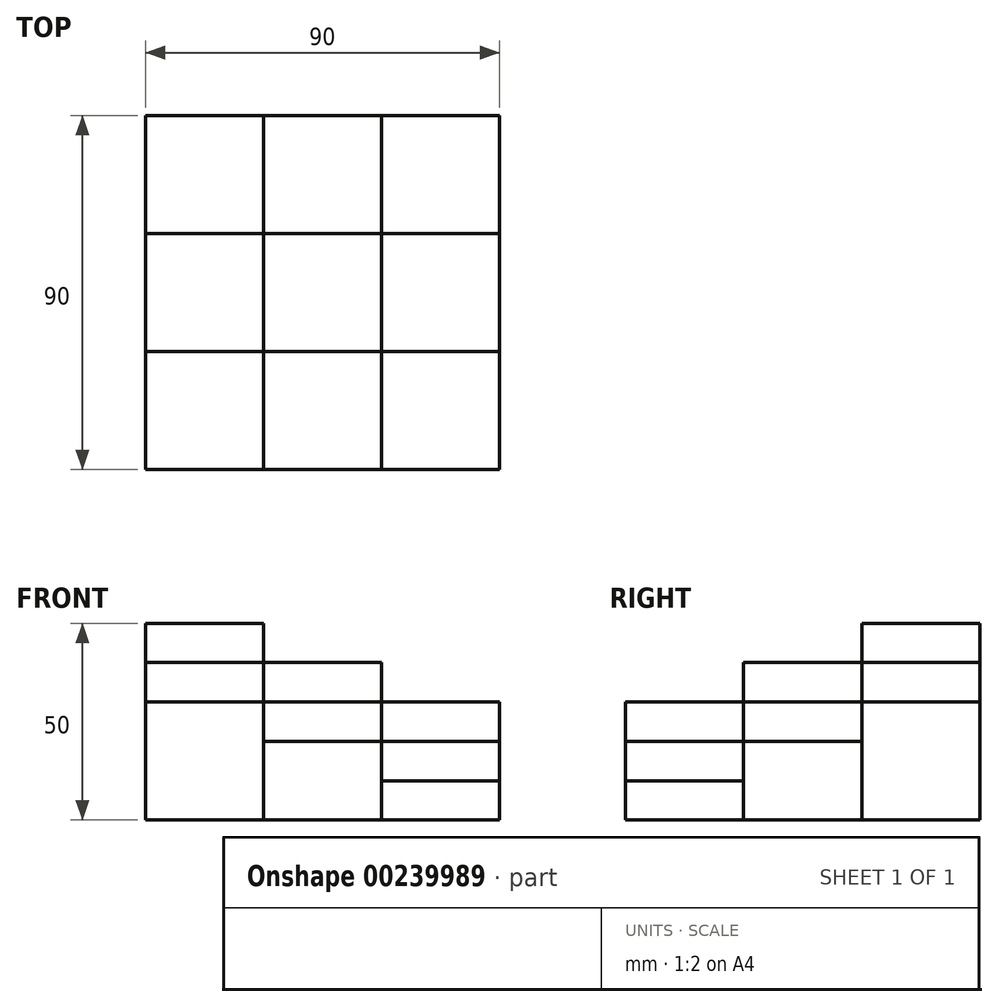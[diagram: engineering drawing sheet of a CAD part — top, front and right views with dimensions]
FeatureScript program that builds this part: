
annotation { "Feature Type Name" : "Feature", "Feature Type Description" : "" }
export const myFeature = defineFeature(function(context is Context, id is Id, definition is map)
    precondition{}
    {
        {
            var Q0;
            Q0=qCreatedBy(makeId("Top.planeOp"),FACE);
            var sketch = newSketch(context, id + "F0", { "sketchPlane" : qUnion([Q0])});
            skLineSegment(sketch, "E0.bottom", {"start": v(-45, 45) * mm, "end": v(45, 45) * mm});
            skLineSegment(sketch, "E0.top", {"start": v(-45, -45) * mm, "end": v(45, -45) * mm});
            skLineSegment(sketch, "E0.left", {"start": v(-45, 45) * mm, "end": v(-45, -45) * mm});
            skLineSegment(sketch, "E0.right", {"start": v(45, 45) * mm, "end": v(45, -45) * mm});
            skPoint(sketch, "E0.middle", {"position": v(0, 0) * mm});
            skLineSegment(sketch, "E1", {"start": v(-45, 15) * mm, "end": v(45, 15) * mm});
            skLineSegment(sketch, "E2", {"start": v(-45, -15) * mm, "end": v(45, -15) * mm});
            skLineSegment(sketch, "E3", {"start": v(-15, 45) * mm, "end": v(-15, -45) * mm});
            skLineSegment(sketch, "E4", {"start": v(15, 45) * mm, "end": v(15, -45) * mm});
            skSolve(sketch);
        }
        {
            var Q0;
            {var subQ0=sQuery(id+"F0.wireOp",EDGE,"E0.right");var subQ1=sQuery(id+"F0.wireOp",EDGE,"E0.top");var subQ2=makeQuery(id+"F0.imprint","INTERSECT",VERTEX,{"derivedFrom":[subQ1,subQ0]});Q0=makeQuery(id+"F0.imprint","IMPRINT",FACE,{"disambiguationData":[TD([[makeQuery(id+"F0.imprint","IMPRINT",EDGE,{"disambiguationData":[TD([[subQ2,1.0]])],"derivedFrom":subQ1}),1.0]])]});}
            extrude(context, id + "F1", {"entities" : qUnion([Q0]), "depth" : 10 * mm});
        }
        {
            var Q0;
            {var subQ0=sQuery(id+"F0.wireOp",EDGE,"E3");var subQ1=sQuery(id+"F0.wireOp",EDGE,"E0.top");var subQ2=makeQuery(id+"F0.imprint","INTERSECT",VERTEX,{"derivedFrom":[subQ1,subQ0]});Q0=makeQuery(id+"F0.imprint","IMPRINT",FACE,{"disambiguationData":[TD([[makeQuery(id+"F0.imprint","IMPRINT",EDGE,{"disambiguationData":[TD([[subQ2,-1.0]])],"derivedFrom":subQ1}),1.0]])]});}
            var Q1;
            {var subQ0=sQuery(id+"F0.wireOp",EDGE,"E1");var subQ1=sQuery(id+"F0.wireOp",EDGE,"E0.right");var subQ2=makeQuery(id+"F0.imprint","INTERSECT",VERTEX,{"derivedFrom":[subQ1,subQ0]});Q1=makeQuery(id+"F0.imprint","IMPRINT",FACE,{"disambiguationData":[TD([[makeQuery(id+"F0.imprint","IMPRINT",EDGE,{"disambiguationData":[TD([[subQ2,-1.0]])],"derivedFrom":subQ1}),-1.0]])]});}
            extrude(context, id + "F2", {"entities" : qUnion([Q0, Q1]), "depth" : 20 * mm});
        }
        {
            var Q0;
            {var subQ0=sQuery(id+"F0.wireOp",EDGE,"E0.left");var subQ1=sQuery(id+"F0.wireOp",EDGE,"E0.top");var subQ2=makeQuery(id+"F0.imprint","INTERSECT",VERTEX,{"derivedFrom":[subQ1,subQ0]});Q0=makeQuery(id+"F0.imprint","IMPRINT",FACE,{"disambiguationData":[TD([[makeQuery(id+"F0.imprint","IMPRINT",EDGE,{"disambiguationData":[TD([[subQ2,-1.0]])],"derivedFrom":subQ1}),1.0]])]});}
            var Q1;
            {var subQ0=sQuery(id+"F0.wireOp",EDGE,"E3");var subQ1=sQuery(id+"F0.wireOp",EDGE,"E1");var subQ2=makeQuery(id+"F0.imprint","INTERSECT",VERTEX,{"derivedFrom":[subQ1,subQ0]});Q1=makeQuery(id+"F0.imprint","IMPRINT",FACE,{"disambiguationData":[TD([[makeQuery(id+"F0.imprint","IMPRINT",EDGE,{"disambiguationData":[TD([[subQ2,-1.0]])],"derivedFrom":subQ1}),-1.0]])]});}
            var Q2;
            {var subQ0=sQuery(id+"F0.wireOp",EDGE,"E0.right");var subQ1=sQuery(id+"F0.wireOp",EDGE,"E0.bottom");var subQ2=makeQuery(id+"F0.imprint","INTERSECT",VERTEX,{"derivedFrom":[subQ1,subQ0]});Q2=makeQuery(id+"F0.imprint","IMPRINT",FACE,{"disambiguationData":[TD([[makeQuery(id+"F0.imprint","IMPRINT",EDGE,{"disambiguationData":[TD([[subQ2,1.0]])],"derivedFrom":subQ1}),-1.0]])]});}
            extrude(context, id + "F3", {"entities" : qUnion([Q0, Q1, Q2]), "depth" : 30 * mm});
        }
        {
            var Q0;
            {var subQ0=sQuery(id+"F0.wireOp",EDGE,"E1");var subQ1=sQuery(id+"F0.wireOp",EDGE,"E0.left");var subQ2=makeQuery(id+"F0.imprint","INTERSECT",VERTEX,{"derivedFrom":[subQ1,subQ0]});Q0=makeQuery(id+"F0.imprint","IMPRINT",FACE,{"disambiguationData":[TD([[makeQuery(id+"F0.imprint","IMPRINT",EDGE,{"disambiguationData":[TD([[subQ2,-1.0]])],"derivedFrom":subQ1}),1.0]])]});}
            var Q1;
            {var subQ0=sQuery(id+"F0.wireOp",EDGE,"E3");var subQ1=sQuery(id+"F0.wireOp",EDGE,"E0.bottom");var subQ2=makeQuery(id+"F0.imprint","INTERSECT",VERTEX,{"derivedFrom":[subQ1,subQ0]});Q1=makeQuery(id+"F0.imprint","IMPRINT",FACE,{"disambiguationData":[TD([[makeQuery(id+"F0.imprint","IMPRINT",EDGE,{"disambiguationData":[TD([[subQ2,-1.0]])],"derivedFrom":subQ1}),-1.0]])]});}
            extrude(context, id + "F4", {"entities" : qUnion([Q0, Q1]), "depth" : 40 * mm});
        }
        {
            var Q0;
            {var subQ0=sQuery(id+"F0.wireOp",EDGE,"E0.left");var subQ1=sQuery(id+"F0.wireOp",EDGE,"E0.bottom");var subQ2=makeQuery(id+"F0.imprint","INTERSECT",VERTEX,{"derivedFrom":[subQ1,subQ0]});Q0=makeQuery(id+"F0.imprint","IMPRINT",FACE,{"disambiguationData":[TD([[makeQuery(id+"F0.imprint","IMPRINT",EDGE,{"disambiguationData":[TD([[subQ2,-1.0]])],"derivedFrom":subQ1}),-1.0]])]});}
            extrude(context, id + "F5", {"entities" : qUnion([Q0]), "depth" : 50 * mm});
        }
    });
